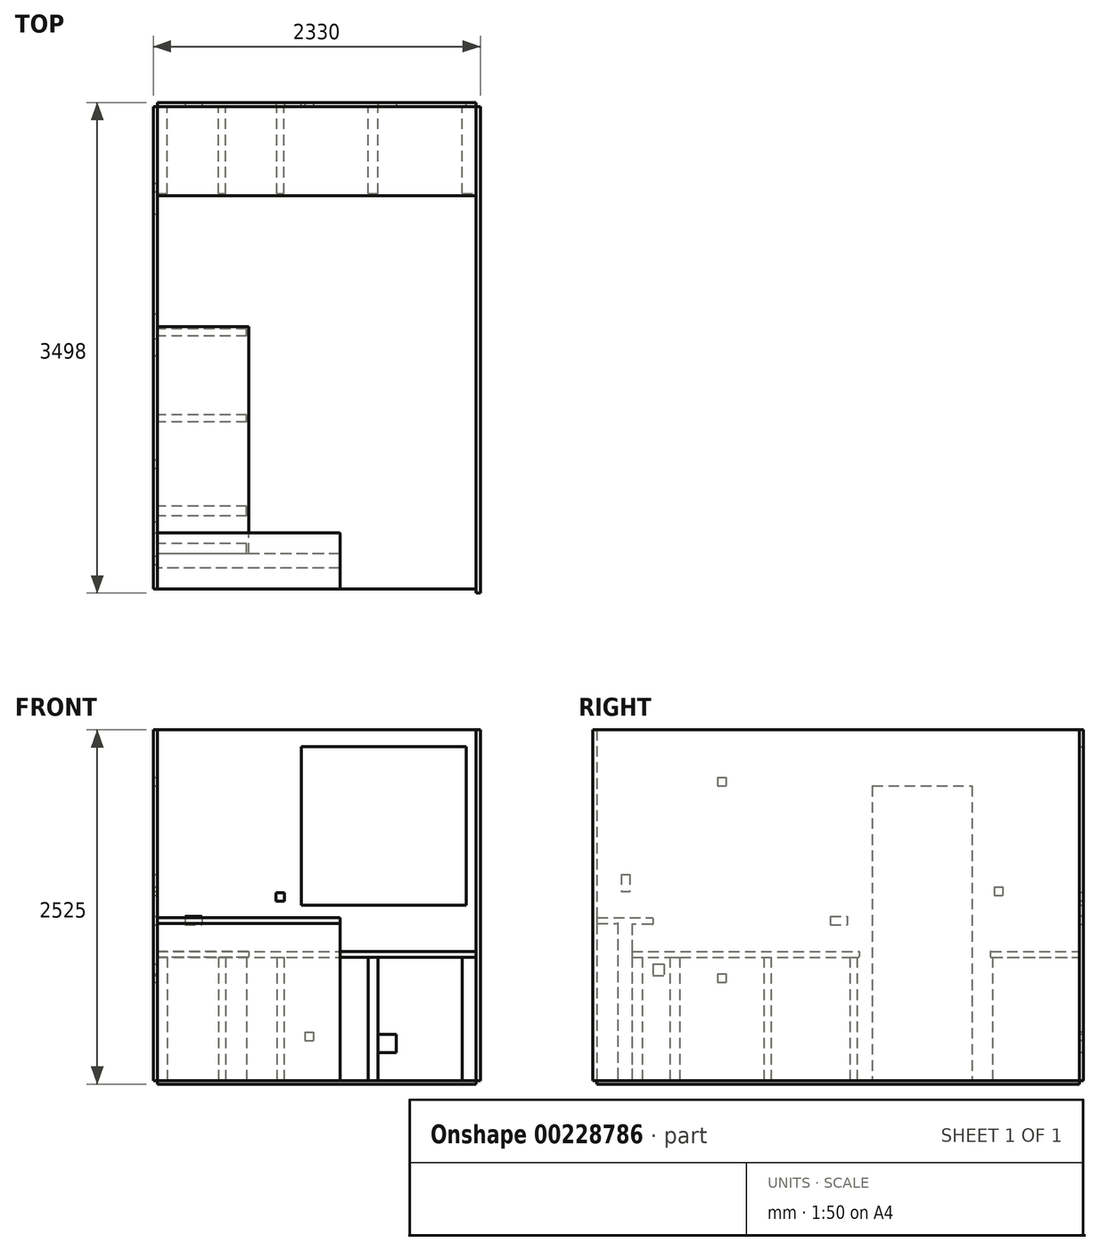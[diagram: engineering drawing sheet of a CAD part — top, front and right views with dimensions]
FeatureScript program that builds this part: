
annotation { "Feature Type Name" : "Feature", "Feature Type Description" : "" }
export const myFeature = defineFeature(function(context is Context, id is Id, definition is map)
    precondition{}
    {
        {
            var Q0;
            Q0=qCreatedBy(makeId("Top.planeOp"),FACE);
            var sketch = newSketch(context, id + "F0", { "sketchPlane" : qUnion([Q0])});
            skLineSegment(sketch, "E0.bottom", {"start": v(-166.7, 1726.55) * mm, "end": v(-136.7, 1726.55) * mm});
            skLineSegment(sketch, "E0.top", {"start": v(-166.7, -1711.45) * mm, "end": v(-136.7, -1711.45) * mm});
            skLineSegment(sketch, "E0.left", {"start": v(-166.7, 1726.55) * mm, "end": v(-166.7, -1711.45) * mm});
            skLineSegment(sketch, "E0.right", {"start": v(-136.7, 1726.55) * mm, "end": v(-136.7, -1711.45) * mm});
            skLineSegment(sketch, "E1.bottom", {"start": v(-136.7, 1756.55) * mm, "end": v(2133.3, 1756.55) * mm});
            skLineSegment(sketch, "E1.top", {"start": v(-136.7, 1726.55) * mm, "end": v(2133.3, 1726.55) * mm});
            skLineSegment(sketch, "E1.left", {"start": v(-136.7, 1756.55) * mm, "end": v(-136.7, 1726.55) * mm});
            skLineSegment(sketch, "E1.right", {"start": v(2133.3, 1756.55) * mm, "end": v(2133.3, 1726.55) * mm});
            skLineSegment(sketch, "E2.bottom", {"start": v(2133.3, 1726.55) * mm, "end": v(2163.3, 1726.55) * mm});
            skLineSegment(sketch, "E2.top", {"start": v(2133.3, -1741.45) * mm, "end": v(2163.3, -1741.45) * mm});
            skLineSegment(sketch, "E2.left", {"start": v(2133.3, 1726.55) * mm, "end": v(2133.3, -1741.45) * mm});
            skLineSegment(sketch, "E2.right", {"start": v(2163.3, 1726.55) * mm, "end": v(2163.3, -1741.45) * mm});
            skLineSegment(sketch, "E3.bottom", {"start": v(-166.7, 961.55) * mm, "end": v(-136.7, 961.55) * mm});
            skLineSegment(sketch, "E3.top", {"start": v(-166.7, 251.55) * mm, "end": v(-136.7, 251.55) * mm});
            skLineSegment(sketch, "E3.left", {"start": v(-166.7, 961.55) * mm, "end": v(-166.7, 251.55) * mm});
            skLineSegment(sketch, "E3.right", {"start": v(-136.7, 961.55) * mm, "end": v(-136.7, 251.55) * mm});
            skSolve(sketch);
        }
        {
            var Q0;
            Q0=makeQuery(id+"F0.imprint","IMPRINT",FACE,{"disambiguationData":[TD([[makeQuery(id+"F0.imprint","IMPRINT",EDGE,{"derivedFrom":sQuery(id+"F0.wireOp",EDGE,"E1.bottom")}),-1.0]])]});
            var Q1;
            Q1=makeQuery(id+"F0.imprint","IMPRINT",FACE,{"disambiguationData":[TD([[makeQuery(id+"F0.imprint","IMPRINT",EDGE,{"derivedFrom":sQuery(id+"F0.wireOp",EDGE,"E2.bottom")}),-1.0]])]});
            var Q2;
            {var subQ0=sQuery(id+"F0.wireOp",EDGE,"E0.bottom");Q2=makeQuery(id+"F0.imprint","IMPRINT",FACE,{"disambiguationData":[TD([[makeQuery(id+"F0.imprint","IMPRINT",EDGE,{"derivedFrom":subQ0}),-1.0]])]});}
            var Q3;
            {var subQ0=sQuery(id+"F0.wireOp",EDGE,"E0.top");Q3=makeQuery(id+"F0.imprint","IMPRINT",FACE,{"disambiguationData":[TD([[makeQuery(id+"F0.imprint","IMPRINT",EDGE,{"derivedFrom":subQ0}),1.0]])]});}
            extrude(context, id + "F1", {"entities" : qUnion([Q0, Q1, Q2, Q3]), "depth" : 2500 * mm});
        }
        {
            var Q0;
            Q0=makeQuery(id+"F1.opExtrude","CAP_FACE",FACE,{"disambiguationData":[OSD([sQuery(id+"F0.wireOp",EDGE,"E0.top"),sQuery(id+"F0.wireOp",EDGE,"E0.left"),sQuery(id+"F0.wireOp",EDGE,"E0.right"),sQuery(id+"F0.wireOp",EDGE,"E3.top")])],"isStart":true});
            var sketch = newSketch(context, id + "F2", { "sketchPlane" : qUnion([Q0])});
            skLineSegment(sketch, "E4.bottom", {"start": v(-136.7, 1711.45) * mm, "end": v(2133.3, 1711.45) * mm});
            skLineSegment(sketch, "E4.top", {"start": v(-136.7, -1726.55) * mm, "end": v(2133.3, -1726.55) * mm});
            skLineSegment(sketch, "E4.left", {"start": v(-136.7, 1711.45) * mm, "end": v(-136.7, -1726.55) * mm});
            skLineSegment(sketch, "E4.right", {"start": v(2133.3, 1711.45) * mm, "end": v(2133.3, -1726.55) * mm});
            skSolve(sketch);
        }
        {
            var Q0;
            Q0=qSketchRegion(id+"F2",true);
            extrude(context, id + "F3", {"entities" : qUnion([Q0]), "depth" : 25 * mm});
        }
        {
            var Q0;
            Q0=makeQuery(id+"F1.opExtrude","SWEPT_FACE",FACE,{"disambiguationData":[OSD([sQuery(id+"F0.wireOp",EDGE,"E1.top")])]});
            var sketch = newSketch(context, id + "F4", { "sketchPlane" : qUnion([Q0])});
            skLineSegment(sketch, "E5.bottom", {"start": v(-136.7, 2500) * mm, "end": v(2133.3, 2500) * mm, "construction": true});
            skLineSegment(sketch, "E5.top", {"start": v(-136.7, 0) * mm, "end": v(2133.3, 0) * mm, "construction": true});
            skLineSegment(sketch, "E5.left", {"start": v(-136.7, 2500) * mm, "end": v(-136.7, 0) * mm, "construction": true});
            skLineSegment(sketch, "E5.right", {"start": v(2133.3, 2500) * mm, "end": v(2133.3, 0) * mm, "construction": true});
            skLineSegment(sketch, "E6", {"start": v(-136.7, 920) * mm, "end": v(2133.3, 920) * mm, "construction": true});
            skLineSegment(sketch, "E7.bottom", {"start": v(-136.7, 920) * mm, "end": v(2133.3, 920) * mm});
            skLineSegment(sketch, "E7.top", {"start": v(-136.7, 880) * mm, "end": v(2133.3, 880) * mm});
            skLineSegment(sketch, "E7.left", {"start": v(-136.7, 920) * mm, "end": v(-136.7, 880) * mm});
            skLineSegment(sketch, "E7.right", {"start": v(2133.3, 920) * mm, "end": v(2133.3, 880) * mm});
            skSolve(sketch);
        }
        {
            var Q0;
            Q0=qSketchRegion(id+"F4",true);
            extrude(context, id + "F5", {"entities" : qUnion([Q0]), "depth" : 635 * mm});
        }
        {
            var Q0;
            {var subQ0=sQuery(id+"F0.wireOp",EDGE,"E0.right");Q0=makeQuery(id+"F1.opExtrude","SWEPT_FACE",FACE,{"disambiguationData":[OSD([subQ0]),TDD([makeQuery(id+"F0.imprint","IMPRINT",EDGE,{"disambiguationData":[TD([[makeQuery(id+"F0.imprint","INTERSECT",VERTEX,{"derivedFrom":[sQuery(id+"F0.wireOp",EDGE,"E0.top"),subQ0]}),1.0]])],"derivedFrom":subQ0})])]});}
            var sketch = newSketch(context, id + "F6", { "sketchPlane" : qUnion([Q0])});
            skLineSegment(sketch, "E8.top", {"start": v(-1461.45, 880) * mm, "end": v(159.45, 880) * mm});
            skLineSegment(sketch, "E8.left", {"start": v(-1461.45, 920) * mm, "end": v(-1461.45, 880) * mm});
            skLineSegment(sketch, "E8.right", {"start": v(159.45, 920) * mm, "end": v(159.45, 880) * mm});
            skLineSegment(sketch, "E9", {"start": v(-1511.45, 1160) * mm, "end": v(-1711.45, 1160) * mm});
            skLineSegment(sketch, "E10", {"start": v(-1711.45, 1120) * mm, "end": v(-1561.45, 1120) * mm});
            skLineSegment(sketch, "E11", {"start": v(-1561.45, 1120) * mm, "end": v(-1561.45, 0) * mm});
            skLineSegment(sketch, "E12.MirrorCS", {"start": v(-1311.45, 1113.32) * mm, "end": v(-1460.49, 1113.32) * mm});
            skLineSegment(sketch, "E13.MirrorCS", {"start": v(-1511.45, 1160) * mm, "end": v(-1311.45, 1160) * mm});
            skLineSegment(sketch, "E14", {"start": v(-1711.45, 1160) * mm, "end": v(-1711.45, 1120) * mm});
            skLineSegment(sketch, "E15", {"start": v(-1311.45, 1160) * mm, "end": v(-1311.45, 1113.32) * mm});
            skLineSegment(sketch, "E16", {"start": v(-1561.45, 0) * mm, "end": v(-1461.45, 0) * mm});
            skLineSegment(sketch, "E17", {"start": v(-1460.55, 920) * mm, "end": v(-1460.55, 880) * mm});
            skLineSegment(sketch, "E18", {"start": v(-1460.55, 920) * mm, "end": v(159.45, 920) * mm});
            skLineSegment(sketch, "E19", {"start": v(-1460.49, 1113.32) * mm, "end": v(-1461.45, 0) * mm});
            skSolve(sketch);
        }
        {
            var Q0;
            Q0=makeQuery(id+"F6.imprint","IMPRINT",FACE,{"disambiguationData":[TD([[makeQuery(id+"F6.imprint","IMPRINT",EDGE,{"derivedFrom":sQuery(id+"F6.wireOp",EDGE,"E9")}),1.0]])]});
            extrude(context, id + "F7", {"entities" : qUnion([Q0]), "depth" : 1300 * mm});
        }
        {
            var Q0;
            {var subQ0=sQuery(id+"F6.wireOp",EDGE,"E8.right");Q0=makeQuery(id+"F6.imprint","IMPRINT",FACE,{"disambiguationData":[TD([[makeQuery(id+"F6.imprint","IMPRINT",EDGE,{"derivedFrom":subQ0}),-1.0]])]});}
            extrude(context, id + "F8", {"entities" : qUnion([Q0]), "operationType" : NewBodyOperationType.ADD, "depth" : 650 * mm});
        }
        {
            var Q0;
            Q0=makeQuery(id+"F1.opExtrude","SWEPT_FACE",FACE,{"disambiguationData":[OSD([sQuery(id+"F0.wireOp",EDGE,"E1.bottom")])]});
            var sketch = newSketch(context, id + "F9", { "sketchPlane" : qUnion([Q0])});
            skLineSegment(sketch, "E20.bottom", {"start": v(-886.3, 2380) * mm, "end": v(-2063.3, 2380) * mm});
            skLineSegment(sketch, "E20.top", {"start": v(-886.3, 1250) * mm, "end": v(-2063.3, 1250) * mm});
            skLineSegment(sketch, "E20.left", {"start": v(-886.3, 2380) * mm, "end": v(-886.3, 1250) * mm});
            skLineSegment(sketch, "E20.right", {"start": v(-2063.3, 2380) * mm, "end": v(-2063.3, 1250) * mm});
            skSolve(sketch);
        }
        {
            var Q0;
            Q0=makeQuery(id+"F9.imprint","IMPRINT",FACE,{"disambiguationData":[TD([[makeQuery(id+"F9.imprint","IMPRINT",EDGE,{"derivedFrom":sQuery(id+"F9.wireOp",EDGE,"E20.bottom")}),1.0]])]});
            extrude(context, id + "F10", {"entities" : qUnion([Q0]), "operationType" : NewBodyOperationType.REMOVE, "endBound" : BoundingType.THROUGH_ALL, "oppositeDirection" : true, "depth" : 25 * mm});
        }
        {
            var Q0;
            Q0=makeQuery(id+"F1.opExtrude","SWEPT_FACE",FACE,{"disambiguationData":[OSD([sQuery(id+"F0.wireOp",EDGE,"E3.bottom")])]});
            var sketch = newSketch(context, id + "F11", { "sketchPlane" : qUnion([Q0])});
            skLineSegment(sketch, "E21.bottom", {"start": v(-166.7, 2500) * mm, "end": v(-136.7, 2500) * mm});
            skLineSegment(sketch, "E21.top", {"start": v(-166.7, 2100) * mm, "end": v(-136.7, 2100) * mm});
            skLineSegment(sketch, "E21.left", {"start": v(-166.7, 2500) * mm, "end": v(-166.7, 2100) * mm});
            skLineSegment(sketch, "E21.right", {"start": v(-136.7, 2500) * mm, "end": v(-136.7, 2100) * mm});
            skSolve(sketch);
        }
        {
            var Q0;
            Q0=makeQuery(id+"F11.imprint","IMPRINT",FACE,{"disambiguationData":[TD([[makeQuery(id+"F11.imprint","IMPRINT",EDGE,{"derivedFrom":sQuery(id+"F11.wireOp",EDGE,"E21.bottom")}),-1.0]])]});
            extrude(context, id + "F12", {"entities" : qUnion([Q0]), "operationType" : NewBodyOperationType.ADD, "depth" : 710 * mm});
        }
        {
            var Q0;
            {var subQ0=sQuery(id+"F0.wireOp",EDGE,"E0.right");Q0=makeQuery(id+"F1.opExtrude","SWEPT_FACE",FACE,{"disambiguationData":[OSD([subQ0]),TDD([makeQuery(id+"F0.imprint","IMPRINT",EDGE,{"disambiguationData":[TD([[makeQuery(id+"F0.imprint","INTERSECT",VERTEX,{"derivedFrom":[sQuery(id+"F0.wireOp",EDGE,"E0.top"),subQ0]}),1.0]])],"derivedFrom":subQ0})])]});}
            var sketch = newSketch(context, id + "F13", { "sketchPlane" : qUnion([Q0])});
            skLineSegment(sketch, "E22", {"start": v(-1997.96, 880) * mm, "end": v(384.41, 880) * mm, "construction": true});
            skLineSegment(sketch, "E23", {"start": v(-1121.45, 0) * mm, "end": v(-1121.45, -0.15) * mm, "construction": true});
            skLineSegment(sketch, "E24.bottom", {"start": v(-1121.45, 880) * mm, "end": v(-1191.45, 880) * mm});
            skLineSegment(sketch, "E24.top", {"start": v(-1121.45, 0) * mm, "end": v(-1191.45, 0) * mm});
            skLineSegment(sketch, "E24.left", {"start": v(-1121.45, 880) * mm, "end": v(-1121.45, 0) * mm});
            skLineSegment(sketch, "E24.right", {"start": v(-1191.45, 880) * mm, "end": v(-1191.45, 0) * mm});
            skLineSegment(sketch, "E25.bottom", {"start": v(-1387.45, 880) * mm, "end": v(-1191.45, 880) * mm});
            skLineSegment(sketch, "E25.top", {"start": v(-1387.45, 0) * mm, "end": v(-1191.45, 0) * mm});
            skLineSegment(sketch, "E25.left", {"start": v(-1387.45, 880) * mm, "end": v(-1387.45, 0) * mm});
            skLineSegment(sketch, "E26.bottom", {"start": v(-1387.45, 880) * mm, "end": v(-1460.55, 880) * mm});
            skLineSegment(sketch, "E26.top", {"start": v(-1387.45, 0) * mm, "end": v(-1460.55, 0) * mm});
            skLineSegment(sketch, "E26.right", {"start": v(-1460.55, 880) * mm, "end": v(-1460.55, 0) * mm});
            skLineSegment(sketch, "E27.bottom", {"start": v(-1121.45, 880) * mm, "end": v(-521.45, 880) * mm});
            skLineSegment(sketch, "E27.top", {"start": v(-1121.45, 0) * mm, "end": v(-521.45, 0) * mm});
            skLineSegment(sketch, "E27.right", {"start": v(-521.45, 880) * mm, "end": v(-521.45, 0) * mm});
            skLineSegment(sketch, "E28.bottom", {"start": v(-521.45, 880) * mm, "end": v(-471.45, 880) * mm});
            skLineSegment(sketch, "E28.top", {"start": v(-521.45, 0) * mm, "end": v(-471.45, 0) * mm});
            skLineSegment(sketch, "E28.right", {"start": v(-471.45, 880) * mm, "end": v(-471.45, 0) * mm});
            skLineSegment(sketch, "E29.bottom", {"start": v(-471.45, 880) * mm, "end": v(92.55, 880) * mm});
            skLineSegment(sketch, "E29.top", {"start": v(-471.45, 0) * mm, "end": v(92.55, 0) * mm});
            skLineSegment(sketch, "E29.right", {"start": v(92.55, 880) * mm, "end": v(92.55, 0) * mm});
            skLineSegment(sketch, "E30.bottom", {"start": v(92.55, 880) * mm, "end": v(142.55, 880) * mm});
            skLineSegment(sketch, "E30.top", {"start": v(92.55, 0) * mm, "end": v(142.55, 0) * mm});
            skLineSegment(sketch, "E30.right", {"start": v(142.55, 880) * mm, "end": v(142.55, 0) * mm});
            skLineSegment(sketch, "E31", {"start": v(-821.45, 2500) * mm, "end": v(-821.45, 0) * mm, "construction": true});
            skSolve(sketch);
        }
        {
            var Q0;
            Q0=makeQuery(id+"F13.imprint","IMPRINT",FACE,{"disambiguationData":[TD([[makeQuery(id+"F13.imprint","IMPRINT",EDGE,{"derivedFrom":sQuery(id+"F13.wireOp",EDGE,"E24.bottom")}),-1.0]])]});
            var Q1;
            Q1=makeQuery(id+"F13.imprint","IMPRINT",FACE,{"disambiguationData":[TD([[makeQuery(id+"F13.imprint","IMPRINT",EDGE,{"derivedFrom":sQuery(id+"F13.wireOp",EDGE,"E26.bottom")}),-1.0]])]});
            var Q2;
            Q2=makeQuery(id+"F13.imprint","IMPRINT",FACE,{"disambiguationData":[TD([[makeQuery(id+"F13.imprint","IMPRINT",EDGE,{"derivedFrom":sQuery(id+"F13.wireOp",EDGE,"E28.bottom")}),-1.0]])]});
            var Q3;
            Q3=makeQuery(id+"F13.imprint","IMPRINT",FACE,{"disambiguationData":[TD([[makeQuery(id+"F13.imprint","IMPRINT",EDGE,{"derivedFrom":sQuery(id+"F13.wireOp",EDGE,"E30.bottom")}),-1.0]])]});
            extrude(context, id + "F14", {"entities" : qUnion([Q0, Q1, Q2, Q3]), "depth" : 635 * mm});
        }
        {
            var Q0;
            Q0=makeQuery(id+"F8.opExtrude","SWEPT_EDGE",EDGE,{"disambiguationData":[OSD([sQuery(id+"F6.wireOp",EDGE,"E8.right"),sQuery(id+"F6.wireOp",EDGE,"E18")])]});
            var Q1;
            Q1=makeQuery(id+"F8.opExtrude","CAP_EDGE",EDGE,{"disambiguationData":[OSD([sQuery(id+"F6.wireOp",EDGE,"E18")])],"isStart":false});
            var Q2;
            Q2=makeQuery(id+"F8.opExtrude","SWEPT_EDGE",EDGE,{"disambiguationData":[OSD([sQuery(id+"F6.wireOp",EDGE,"E8.top"),sQuery(id+"F6.wireOp",EDGE,"E8.right")])]});
            var Q3;
            Q3=makeQuery(id+"F8.opExtrude","CAP_EDGE",EDGE,{"disambiguationData":[OSD([sQuery(id+"F6.wireOp",EDGE,"E8.top")])],"isStart":false});
            fillet(context, id + "F15", {"entities" : qUnion([Q0, Q1, Q2, Q3]), "radius" : 5 * mm, "tangentPropagation" : true, "allowEdgeOverflow" : false});
        }
        {
            var Q0;
            Q0=makeQuery(id+"F7.opExtrude","SWEPT_EDGE",EDGE,{"disambiguationData":[OSD([sQuery(id+"F0.wireOp",EDGE,"E0.top"),sQuery(id+"F0.wireOp",EDGE,"E0.right"),sQuery(id+"F6.wireOp",EDGE,"E9"),sQuery(id+"F6.wireOp",EDGE,"E14")])]});
            var Q1;
            Q1=makeQuery(id+"F7.opExtrude","SWEPT_EDGE",EDGE,{"disambiguationData":[OSD([sQuery(id+"F6.wireOp",EDGE,"E13.MirrorCS"),sQuery(id+"F6.wireOp",EDGE,"E15")])]});
            var Q2;
            Q2=makeQuery(id+"F7.opExtrude","CAP_EDGE",EDGE,{"disambiguationData":[OSD([sQuery(id+"F6.wireOp",EDGE,"E9"),sQuery(id+"F6.wireOp",EDGE,"E13.MirrorCS")])],"isStart":false});
            var Q3;
            Q3=makeQuery(id+"F7.opExtrude","SWEPT_EDGE",EDGE,{"disambiguationData":[OSD([sQuery(id+"F0.wireOp",EDGE,"E0.top"),sQuery(id+"F0.wireOp",EDGE,"E0.right"),sQuery(id+"F6.wireOp",EDGE,"E10"),sQuery(id+"F6.wireOp",EDGE,"E14")])]});
            var Q4;
            Q4=makeQuery(id+"F7.opExtrude","CAP_EDGE",EDGE,{"disambiguationData":[OSD([sQuery(id+"F6.wireOp",EDGE,"E10")])],"isStart":false});
            var Q5;
            Q5=makeQuery(id+"F7.opExtrude","CAP_EDGE",EDGE,{"disambiguationData":[OSD([sQuery(id+"F6.wireOp",EDGE,"E12.MirrorCS")])],"isStart":false});
            var Q6;
            Q6=makeQuery(id+"F7.opExtrude","CAP_EDGE",EDGE,{"disambiguationData":[OSD([sQuery(id+"F6.wireOp",EDGE,"E14")])],"isStart":false});
            var Q7;
            Q7=makeQuery(id+"F7.opExtrude","CAP_EDGE",EDGE,{"disambiguationData":[OSD([sQuery(id+"F6.wireOp",EDGE,"E15")])],"isStart":false});
            var Q8;
            Q8=makeQuery(id+"F7.opExtrude","SWEPT_EDGE",EDGE,{"disambiguationData":[OSD([sQuery(id+"F6.wireOp",EDGE,"E12.MirrorCS"),sQuery(id+"F6.wireOp",EDGE,"E15")])]});
            fillet(context, id + "F16", {"entities" : qUnion([Q0, Q1, Q2, Q3, Q4, Q5, Q6, Q7, Q8]), "radius" : 5 * mm, "tangentPropagation" : true, "allowEdgeOverflow" : false});
        }
        {
            var Q0;
            Q0=makeQuery(id+"F5.opExtrude","CAP_EDGE",EDGE,{"disambiguationData":[OSD([sQuery(id+"F4.wireOp",EDGE,"E7.bottom")])],"isStart":false});
            var Q1;
            Q1=makeQuery(id+"F5.opExtrude","CAP_EDGE",EDGE,{"disambiguationData":[OSD([sQuery(id+"F4.wireOp",EDGE,"E7.top")])],"isStart":false});
            fillet(context, id + "F17", {"entities" : qUnion([Q0, Q1]), "radius" : 5 * mm, "tangentPropagation" : true, "allowEdgeOverflow" : false});
        }
        {
            var Q0;
            {var subQ0=sQuery(id+"F4.wireOp",EDGE,"E7.top");Q0=makeQuery(id+"F4.imprint","IMPRINT",FACE,{"disambiguationData":[TD([[makeQuery(id+"F4.imprint","IMPRINT",EDGE,{"derivedFrom":subQ0}),-1.0]])]});}
            var sketch = newSketch(context, id + "F18", { "sketchPlane" : qUnion([Q0])});
            skLineSegment(sketch, "E32", {"start": v(-136.7, 0) * mm, "end": v(-136.7, 880) * mm, "construction": true});
            skLineSegment(sketch, "E33", {"start": v(2133.3, 0) * mm, "end": v(2133.3, 880) * mm, "construction": true});
            skLineSegment(sketch, "E34", {"start": v(-136.7, 880) * mm, "end": v(2133.3, 880) * mm, "construction": true});
            skLineSegment(sketch, "E35.bottom", {"start": v(2133.3, 880) * mm, "end": v(2033.3, 880) * mm});
            skLineSegment(sketch, "E35.top", {"start": v(2133.3, 0) * mm, "end": v(2033.3, 0) * mm});
            skLineSegment(sketch, "E35.left", {"start": v(2133.3, 880) * mm, "end": v(2133.3, 0) * mm});
            skLineSegment(sketch, "E35.right", {"start": v(2033.3, 880) * mm, "end": v(2033.3, 0) * mm});
            skLineSegment(sketch, "E36.bottom", {"start": v(1433.3, 880) * mm, "end": v(1363.3, 880) * mm});
            skLineSegment(sketch, "E36.top", {"start": v(1433.3, 0) * mm, "end": v(1363.3, 0) * mm});
            skLineSegment(sketch, "E36.left", {"start": v(1433.3, 880) * mm, "end": v(1433.3, 0) * mm});
            skLineSegment(sketch, "E36.right", {"start": v(1363.3, 880) * mm, "end": v(1363.3, 0) * mm});
            skLineSegment(sketch, "E37.bottom", {"start": v(713.3, 880) * mm, "end": v(763.3, 880) * mm});
            skLineSegment(sketch, "E37.top", {"start": v(713.3, 0) * mm, "end": v(763.3, 0) * mm});
            skLineSegment(sketch, "E37.left", {"start": v(713.3, 880) * mm, "end": v(713.3, 0) * mm});
            skLineSegment(sketch, "E37.right", {"start": v(763.3, 880) * mm, "end": v(763.3, 0) * mm});
            skLineSegment(sketch, "E38.bottom", {"start": v(-136.7, 880) * mm, "end": v(-66.7, 880) * mm});
            skLineSegment(sketch, "E38.top", {"start": v(-136.7, 0) * mm, "end": v(-66.7, 0) * mm});
            skLineSegment(sketch, "E38.left", {"start": v(-136.7, 880) * mm, "end": v(-136.7, 0) * mm});
            skLineSegment(sketch, "E38.right", {"start": v(-66.7, 880) * mm, "end": v(-66.7, 0) * mm});
            skLineSegment(sketch, "E39.bottom", {"start": v(297.3, 880) * mm, "end": v(349.3, 880) * mm});
            skLineSegment(sketch, "E39.top", {"start": v(297.3, 0) * mm, "end": v(349.3, 0) * mm});
            skLineSegment(sketch, "E39.left", {"start": v(297.3, 880) * mm, "end": v(297.3, 0) * mm});
            skLineSegment(sketch, "E39.right", {"start": v(349.3, 880) * mm, "end": v(349.3, 0) * mm});
            skSolve(sketch);
        }
        {
            var Q0;
            Q0=qSketchRegion(id+"F18",true);
            extrude(context, id + "F19", {"entities" : qUnion([Q0]), "depth" : 620 * mm});
        }
        {
            var Q0;
            {var subQ0=sQuery(id+"F0.wireOp",EDGE,"E0.right");Q0=makeQuery(id+"F1.opExtrude","SWEPT_FACE",FACE,{"disambiguationData":[OSD([subQ0]),TDD([makeQuery(id+"F0.imprint","IMPRINT",EDGE,{"disambiguationData":[TD([[makeQuery(id+"F0.imprint","INTERSECT",VERTEX,{"derivedFrom":[sQuery(id+"F0.wireOp",EDGE,"E0.top"),subQ0]}),1.0]])],"derivedFrom":subQ0})])]});}
            var sketch = newSketch(context, id + "F20", { "sketchPlane" : qUnion([Q0])});
            skLineSegment(sketch, "E40.bottom", {"start": v(-1536.45, 1470) * mm, "end": v(-1476.45, 1470) * mm});
            skLineSegment(sketch, "E40.top", {"start": v(-1536.45, 1350) * mm, "end": v(-1476.45, 1350) * mm});
            skLineSegment(sketch, "E40.left", {"start": v(-1536.45, 1470) * mm, "end": v(-1536.45, 1350) * mm});
            skLineSegment(sketch, "E40.right", {"start": v(-1476.45, 1470) * mm, "end": v(-1476.45, 1350) * mm});
            skLineSegment(sketch, "E41.bottom", {"start": v(-851.45, 2160) * mm, "end": v(-791.45, 2160) * mm});
            skLineSegment(sketch, "E41.top", {"start": v(-851.45, 2100) * mm, "end": v(-791.45, 2100) * mm});
            skLineSegment(sketch, "E41.left", {"start": v(-851.45, 2160) * mm, "end": v(-851.45, 2100) * mm});
            skLineSegment(sketch, "E41.right", {"start": v(-791.45, 2160) * mm, "end": v(-791.45, 2100) * mm});
            skLineSegment(sketch, "E42.bottom", {"start": v(-1311.45, 830) * mm, "end": v(-1231.45, 830) * mm});
            skLineSegment(sketch, "E42.top", {"start": v(-1311.45, 750) * mm, "end": v(-1231.45, 750) * mm});
            skLineSegment(sketch, "E42.left", {"start": v(-1311.45, 830) * mm, "end": v(-1311.45, 750) * mm});
            skLineSegment(sketch, "E42.right", {"start": v(-1231.45, 830) * mm, "end": v(-1231.45, 750) * mm});
            skLineSegment(sketch, "E43.bottom", {"start": v(-851.45, 760) * mm, "end": v(-791.45, 760) * mm});
            skLineSegment(sketch, "E43.top", {"start": v(-851.45, 700) * mm, "end": v(-791.45, 700) * mm});
            skLineSegment(sketch, "E43.left", {"start": v(-851.45, 760) * mm, "end": v(-851.45, 700) * mm});
            skLineSegment(sketch, "E43.right", {"start": v(-791.45, 760) * mm, "end": v(-791.45, 700) * mm});
            skLineSegment(sketch, "E44.bottom", {"start": v(1121.55, 1380) * mm, "end": v(1181.55, 1380) * mm});
            skLineSegment(sketch, "E44.top", {"start": v(1121.55, 1320) * mm, "end": v(1181.55, 1320) * mm});
            skLineSegment(sketch, "E44.left", {"start": v(1121.55, 1380) * mm, "end": v(1121.55, 1320) * mm});
            skLineSegment(sketch, "E44.right", {"start": v(1181.55, 1380) * mm, "end": v(1181.55, 1320) * mm});
            skLineSegment(sketch, "E45", {"start": v(-1711.45, 0) * mm, "end": v(1987.19, 0) * mm, "construction": true});
            skLineSegment(sketch, "E46", {"start": v(-1711.45, 0) * mm, "end": v(-1711.45, 2805.26) * mm, "construction": true});
            skLineSegment(sketch, "E47.bottom", {"start": v(-48.45, 1170) * mm, "end": v(71.55, 1170) * mm});
            skLineSegment(sketch, "E47.top", {"start": v(-48.45, 1110) * mm, "end": v(71.55, 1110) * mm});
            skLineSegment(sketch, "E47.left", {"start": v(-48.45, 1170) * mm, "end": v(-48.45, 1110) * mm});
            skLineSegment(sketch, "E47.right", {"start": v(71.55, 1170) * mm, "end": v(71.55, 1110) * mm});
            skSolve(sketch);
        }
        {
            var Q0;
            Q0 = qSketchRegion(id + "F20", true);
            extrude(context, id + "F21", {"entities" : qUnion([Q0]), "operationType" : NewBodyOperationType.REMOVE, "oppositeDirection" : true, "depth" : 25 * mm});
        }
        {
            var Q0;
            {var subQ0=sQuery(id+"F4.wireOp",EDGE,"E7.bottom");Q0=makeQuery(id+"F4.imprint","IMPRINT",FACE,{"disambiguationData":[TD([[makeQuery(id+"F4.imprint","IMPRINT",EDGE,{"derivedFrom":subQ0}),1.0]])]});}
            var sketch = newSketch(context, id + "F22", { "sketchPlane" : qUnion([Q0])});
            skLineSegment(sketch, "E48.bottom", {"start": v(708.3, 1340) * mm, "end": v(768.3, 1340) * mm});
            skLineSegment(sketch, "E48.top", {"start": v(708.3, 1280) * mm, "end": v(768.3, 1280) * mm});
            skLineSegment(sketch, "E48.left", {"start": v(708.3, 1340) * mm, "end": v(708.3, 1280) * mm});
            skLineSegment(sketch, "E48.right", {"start": v(768.3, 1340) * mm, "end": v(768.3, 1280) * mm});
            skLineSegment(sketch, "E49.bottom", {"start": v(58.3, 1170) * mm, "end": v(178.3, 1170) * mm});
            skLineSegment(sketch, "E49.top", {"start": v(58.3, 1110) * mm, "end": v(178.3, 1110) * mm});
            skLineSegment(sketch, "E49.left", {"start": v(58.3, 1170) * mm, "end": v(58.3, 1110) * mm});
            skLineSegment(sketch, "E49.right", {"start": v(178.3, 1170) * mm, "end": v(178.3, 1110) * mm});
            skLineSegment(sketch, "E50.bottom", {"start": v(913.3, 345) * mm, "end": v(973.3, 345) * mm});
            skLineSegment(sketch, "E50.top", {"start": v(913.3, 285) * mm, "end": v(973.3, 285) * mm});
            skLineSegment(sketch, "E50.left", {"start": v(973.3, 345) * mm, "end": v(973.3, 285) * mm});
            skLineSegment(sketch, "E50.right", {"start": v(913.3, 345) * mm, "end": v(913.3, 285) * mm});
            skLineSegment(sketch, "E51", {"start": v(-140.07, 0) * mm, "end": v(2300.72, 0) * mm, "construction": true});
            skLineSegment(sketch, "E52.bottom", {"start": v(1433.3, 330) * mm, "end": v(1563.3, 330) * mm});
            skLineSegment(sketch, "E52.top", {"start": v(1433.3, 200) * mm, "end": v(1563.3, 200) * mm});
            skLineSegment(sketch, "E52.left", {"start": v(1433.3, 330) * mm, "end": v(1433.3, 200) * mm});
            skLineSegment(sketch, "E52.right", {"start": v(1563.3, 330) * mm, "end": v(1563.3, 200) * mm});
            skSolve(sketch);
        }
        {
            var Q0;
            Q0 = qSketchRegion(id + "F22", true);
            extrude(context, id + "F23", {"entities" : qUnion([Q0]), "operationType" : NewBodyOperationType.REMOVE, "oppositeDirection" : true, "depth" : 25 * mm});
        }
        {
            var Q0;
            Q0=makeQuery(id+"F22.imprint","IMPRINT",FACE,{"disambiguationData":[TD([[makeQuery(id+"F22.imprint","IMPRINT",EDGE,{"derivedFrom":sQuery(id+"F22.wireOp",EDGE,"E52.bottom")}),-1.0]])]});
            extrude(context, id + "F24", {"entities" : qUnion([Q0]), "operationType" : NewBodyOperationType.REMOVE, "oppositeDirection" : true, "depth" : 100 * mm});
        }
    });
